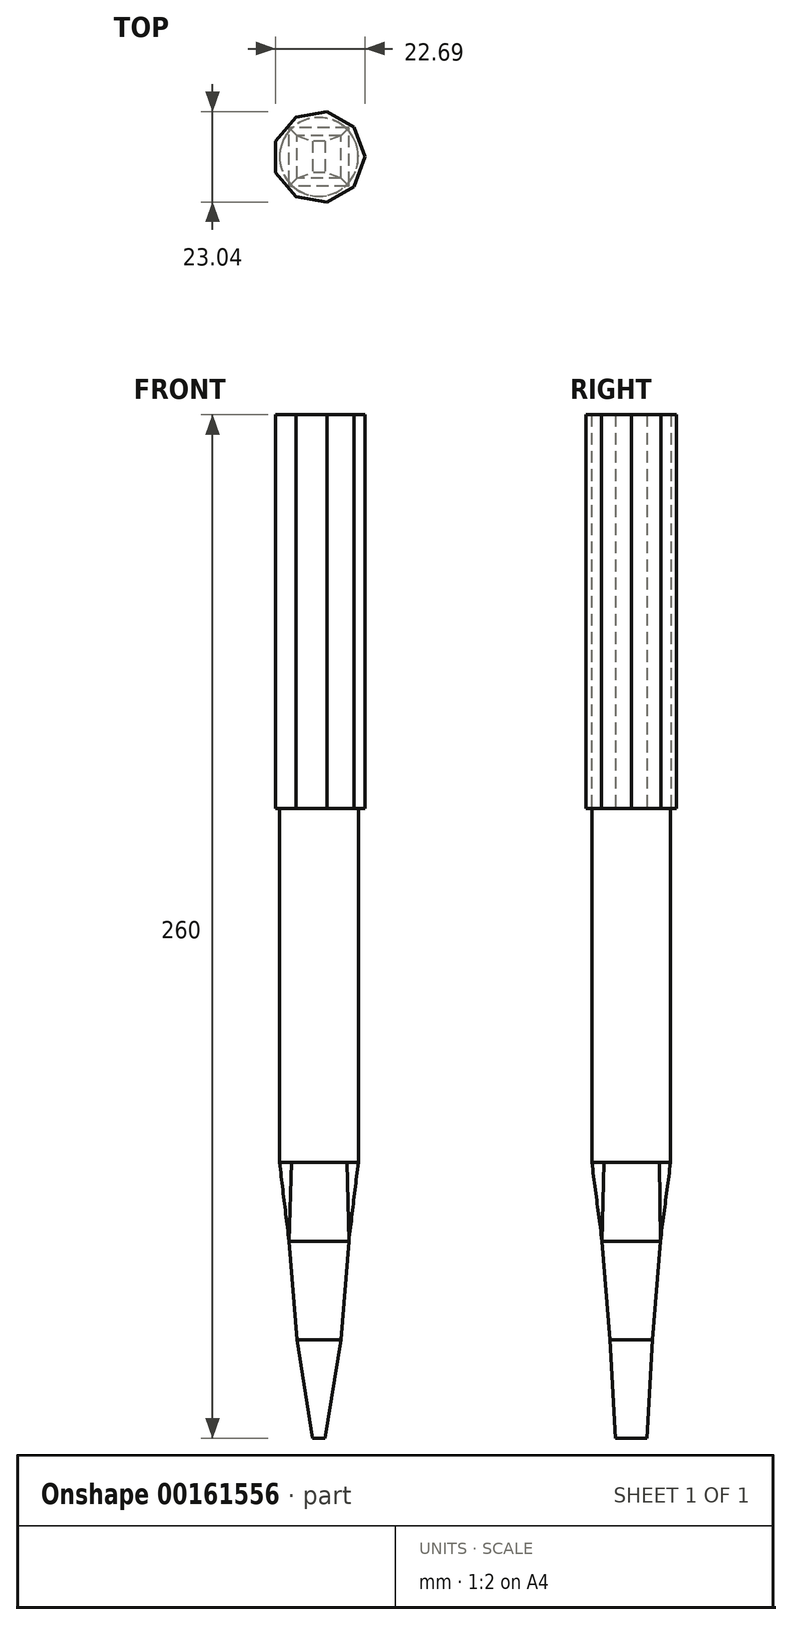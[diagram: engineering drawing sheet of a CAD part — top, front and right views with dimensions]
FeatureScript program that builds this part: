
annotation { "Feature Type Name" : "Feature", "Feature Type Description" : "" }
export const myFeature = defineFeature(function(context is Context, id is Id, definition is map)
    precondition{}
    {
        {
            var Q0;
            Q0=qCreatedBy(makeId("Top.planeOp"),FACE);
            var sketch = newSketch(context, id + "F0", { "sketchPlane" : qUnion([Q0])});
            skCircle(sketch, "E0.cCircle", {"center": v(0, 0) * mm, "radius": 10.99 * mm, "construction": true});
            skLineSegment(sketch, "E0.0", {"start": v(-10.99, -4) * mm, "end": v(-10.99, 4) * mm});
            skLineSegment(sketch, "E0.1", {"start": v(-10.99, 4) * mm, "end": v(-5.85, 10.13) * mm});
            skLineSegment(sketch, "E0.2", {"start": v(-5.85, 10.13) * mm, "end": v(2.03, 11.52) * mm});
            skLineSegment(sketch, "E0.3", {"start": v(2.03, 11.52) * mm, "end": v(8.96, 7.52) * mm});
            skLineSegment(sketch, "E0.4", {"start": v(8.96, 7.52) * mm, "end": v(11.7, 0) * mm});
            skLineSegment(sketch, "E0.5", {"start": v(11.7, 0) * mm, "end": v(8.96, -7.52) * mm});
            skLineSegment(sketch, "E0.6", {"start": v(8.96, -7.52) * mm, "end": v(2.03, -11.52) * mm});
            skLineSegment(sketch, "E0.7", {"start": v(2.03, -11.52) * mm, "end": v(-5.85, -10.13) * mm});
            skLineSegment(sketch, "E0.8", {"start": v(-5.85, -10.13) * mm, "end": v(-10.99, -4) * mm});
            skSolve(sketch);
        }
        {
            var Q0;
            Q0 = qSketchRegion(id + "F0", true);
            extrude(context, id + "F1", {"entities" : qUnion([Q0]), "endBound" : BoundingType.SYMMETRIC, "depth" : 100 * mm});
        }
        {
            var Q0;
            Q0=makeQuery(id+"F1.opExtrude","CAP_FACE",FACE,{"disambiguationData":[OSD([sQuery(id+"F0.wireOp",EDGE,"E0.0"),sQuery(id+"F0.wireOp",EDGE,"E0.1"),sQuery(id+"F0.wireOp",EDGE,"E0.2"),sQuery(id+"F0.wireOp",EDGE,"E0.3"),sQuery(id+"F0.wireOp",EDGE,"E0.4"),sQuery(id+"F0.wireOp",EDGE,"E0.5"),sQuery(id+"F0.wireOp",EDGE,"E0.6"),sQuery(id+"F0.wireOp",EDGE,"E0.7"),sQuery(id+"F0.wireOp",EDGE,"E0.8")])],"isStart":true});
            cPlane(context, id + "F2", {"entities" : qUnion([Q0]), "cplaneType" : CPlaneType.OFFSET, "offset" : 90 * mm, "width" : 150 * mm, "height" : 150 * mm});
        }
        {
            var Q0;
            Q0=qCreatedBy(id+"F2.planeOp",FACE);
            var sketch = newSketch(context, id + "F3", { "sketchPlane" : qUnion([Q0])});
            skCircle(sketch, "E1", {"center": v(0, 0) * mm, "radius": 10 * mm});
            skSolve(sketch);
        }
        {
            var Q0;
            Q0=makeQuery(id+"F1.opExtrude","CAP_FACE",FACE,{"disambiguationData":[OSD([sQuery(id+"F0.wireOp",EDGE,"E0.0"),sQuery(id+"F0.wireOp",EDGE,"E0.1"),sQuery(id+"F0.wireOp",EDGE,"E0.2"),sQuery(id+"F0.wireOp",EDGE,"E0.3"),sQuery(id+"F0.wireOp",EDGE,"E0.4"),sQuery(id+"F0.wireOp",EDGE,"E0.5"),sQuery(id+"F0.wireOp",EDGE,"E0.6"),sQuery(id+"F0.wireOp",EDGE,"E0.7"),sQuery(id+"F0.wireOp",EDGE,"E0.8")])],"isStart":true});
            var sketch = newSketch(context, id + "F4", { "sketchPlane" : qUnion([Q0])});
            skCircle(sketch, "E2", {"center": v(0, 0) * mm, "radius": 10 * mm});
            skSolve(sketch);
        }
        {
            var Q1;
            Q1 = qSketchRegion(id + "F3", true);
            var Q2;
            Q2 = qSketchRegion(id + "F4", true);
            loft(context, id + "F5", {"sheetProfilesArray" : [{ "sheetProfileEntities" : qUnion([Q1]) }, { "sheetProfileEntities" : qUnion([Q2]) }]});
        }
        {
            var Q0;
            Q0=makeQuery(id+"F5.opLoft","CAP_FACE",FACE,{"disambiguationData":[OSD([makeQuery(id+"F3.imprint","IMPRINT",FACE,{"disambiguationData":[TD([[makeQuery(id+"F3.imprint","IMPRINT",EDGE,{"derivedFrom":sQuery(id+"F3.wireOp",EDGE,"E1")}),1.0]])]})])],"isStart":true});
            cPlane(context, id + "F6", {"entities" : qUnion([Q0]), "cplaneType" : CPlaneType.OFFSET, "offset" : 20 * mm, "width" : 150 * mm, "height" : 150 * mm});
        }
        {
            var Q0;
            Q0=qCreatedBy(id+"F6.planeOp",FACE);
            var sketch = newSketch(context, id + "F7", { "sketchPlane" : qUnion([Q0])});
            skLineSegment(sketch, "E3.bottom", {"start": v(7.6, 7.4) * mm, "end": v(-7.6, 7.4) * mm});
            skLineSegment(sketch, "E3.top", {"start": v(7.6, -7.4) * mm, "end": v(-7.6, -7.4) * mm});
            skLineSegment(sketch, "E3.left", {"start": v(7.6, 7.4) * mm, "end": v(7.6, -7.4) * mm});
            skLineSegment(sketch, "E3.right", {"start": v(-7.6, 7.4) * mm, "end": v(-7.6, -7.4) * mm});
            skPoint(sketch, "E3.middle", {"position": v(0, 0) * mm});
            skSolve(sketch);
        }
        {
            var Q1;
            Q1 = qSketchRegion(id + "F3", true);
            var Q2;
            Q2 = qSketchRegion(id + "F7", true);
            loft(context, id + "F8", {"operationType" : NewBodyOperationType.ADD, "sheetProfilesArray" : [{ "sheetProfileEntities" : qUnion([Q1]) }, { "sheetProfileEntities" : qUnion([Q2]) }]});
        }
        {
            var Q0;
            Q0=qCreatedBy(id+"F6.planeOp",FACE);
            cPlane(context, id + "F9", {"entities" : qUnion([Q0]), "cplaneType" : CPlaneType.OFFSET, "offset" : 25 * mm, "width" : 150 * mm, "height" : 150 * mm});
        }
        {
            var Q0;
            Q0=qCreatedBy(id+"F9.planeOp",FACE);
            var sketch = newSketch(context, id + "F10", { "sketchPlane" : qUnion([Q0])});
            skLineSegment(sketch, "E4.bottom", {"start": v(5.6, 5.4) * mm, "end": v(-5.6, 5.4) * mm});
            skLineSegment(sketch, "E4.top", {"start": v(5.6, -5.4) * mm, "end": v(-5.6, -5.4) * mm});
            skLineSegment(sketch, "E4.left", {"start": v(5.6, 5.4) * mm, "end": v(5.6, -5.4) * mm});
            skLineSegment(sketch, "E4.right", {"start": v(-5.6, 5.4) * mm, "end": v(-5.6, -5.4) * mm});
            skPoint(sketch, "E4.middle", {"position": v(0, 0) * mm});
            skSolve(sketch);
        }
        {
            var Q1;
            Q1 = qSketchRegion(id + "F7", true);
            var Q2;
            Q2 = qSketchRegion(id + "F10", true);
            loft(context, id + "F11", {"operationType" : NewBodyOperationType.ADD, "sheetProfilesArray" : [{ "sheetProfileEntities" : qUnion([Q1]) }, { "sheetProfileEntities" : qUnion([Q2]) }]});
        }
        {
            var Q0;
            Q0=qCreatedBy(id+"F9.planeOp",FACE);
            cPlane(context, id + "F12", {"entities" : qUnion([Q0]), "cplaneType" : CPlaneType.OFFSET, "offset" : 25 * mm, "width" : 150 * mm, "height" : 150 * mm});
        }
        {
            var Q0;
            Q0=qCreatedBy(id+"F12.planeOp",FACE);
            var sketch = newSketch(context, id + "F13", { "sketchPlane" : qUnion([Q0])});
            skLineSegment(sketch, "E5.bottom", {"start": v(1.6, -4) * mm, "end": v(-1.6, -4) * mm});
            skLineSegment(sketch, "E5.top", {"start": v(1.6, 4) * mm, "end": v(-1.6, 4) * mm});
            skLineSegment(sketch, "E5.left", {"start": v(1.6, -4) * mm, "end": v(1.6, 4) * mm});
            skLineSegment(sketch, "E5.right", {"start": v(-1.6, -4) * mm, "end": v(-1.6, 4) * mm});
            skPoint(sketch, "E5.middle", {"position": v(0, 0) * mm});
            skSolve(sketch);
        }
        {
            var Q1;
            Q1 = qSketchRegion(id + "F10", true);
            var Q2;
            Q2 = qSketchRegion(id + "F13", true);
            loft(context, id + "F14", {"operationType" : NewBodyOperationType.ADD, "sheetProfilesArray" : [{ "sheetProfileEntities" : qUnion([Q1]) }, { "sheetProfileEntities" : qUnion([Q2]) }]});
        }
    });
